# Revit family: xxxSink-Hand_Hygiene-Franke-Nightingale-AHWSS1720W-00
name_source: partatom
category: Plumbing Fixtures
units: mm (PartAtom-declared; Revit-internal decimal feet)

## family parameters
Cut with Voids When Loaded = No
Host = Face
OmniClass Number = 23.45.05.14.14
OmniClass Title = Sinks/Lavatories
Part Type = Normal
Room Calculation Point = No
Round Connector Dimension = Use Diameter
Shared = Yes

## types (1)
- AHWSS1720W-00
    ADA Compliant = Yes
    ASME A112.18.1/CSA B125.1 = Yes
    Assembly Code = D2010400
    Basin Type = Single Compartment
    Battery Pack Included = No
    Bowl Depth = 15 1/4"
    Bowl Front to Back = 9"
    Bowl Width = 18 9/16"
    CW Connection = Yes
    CWFU = 3
    Cold Water Connection Diameter = 3/8"
    Cold Water Connection Height = 20"
    Cold Water Connection Width = 4"
    Compliance Certifications = CSA B45.5-11/IAPMO Z124-2011, CSAZ8000, CSAZ317.1-16, ANSI A117.1 and CSA B651-04
    Default Elevation = 34"
    Description = Healthcare AHWSS1720W-00 Nightingale Sink
    Finish = Synthetic-Franke-Miranit-White-High Polished
    Finish- Faucet = Metal-Franke
    Flow Rate = 4L/min (1.05 GPM), Low flow @ 1 L/min (0.26gpm)
    HW Connection = Yes
    HWFU = 3
    Height = 21 9/16"
    Hot Water Connection Diameter = 3/8"
    Hot Water Connection Height = 20"
    Hot Water Connection Width = 4"
    Installation Type = Wall Mount
    Length = 16 15/16"
    Manufacturer = Franke
    Material = Synthetic-Franke-Miranit-White-High Polished
    Model = AHWSS1720W-00
    Optional MIX-LF Thermostatic Mixing Valve = No
    Plug-in Transformer Included = Yes
    Price = Prices may vary. Please consult Manufacturer Representative for most up-to-date price list.
    Product Documentation Link = https://franke-ws-data.mycontent.ch
    Product Page URL = https://www.franke.com
    URL = https://www.franke.com
    Vent Connection = No
    WFU = 4
    Waste Connection = Yes
    Waste Connection Diameter = 1 1/2"
    Waste Connection Height = 18"
    Width = 20 1/8"
    cUPC Compliant = Yes

## geometry (parser evidence)
native form markers: Sweep x2
no freeform markers — native parametric forms only
